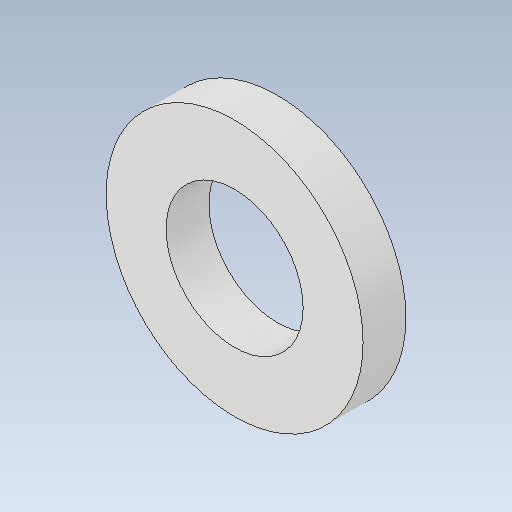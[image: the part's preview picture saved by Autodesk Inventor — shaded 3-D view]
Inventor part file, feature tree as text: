
AUTODESK INVENTOR PART (.ipt)
format: ipt  version: 2020.2 (Build 242310000, 310)  size: 99,840 bytes
history: native  units: mm
features: other x1, extrude x1, sketch x1
ambient origin geometry x8: Origin, YZ Plane, XZ Plane, XY Plane, X Axis, Y Axis, Z Axis, Center Point
bodies: Body1 (feature_tree)
feature tree (3):
  other  "ソリッド1"
  extrude  "押し出し1"  Depth=3.2mm
  sketch  "スケッチ1"
